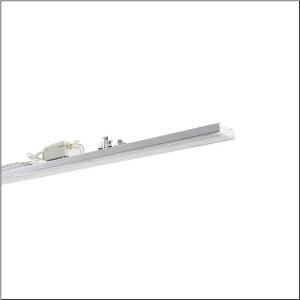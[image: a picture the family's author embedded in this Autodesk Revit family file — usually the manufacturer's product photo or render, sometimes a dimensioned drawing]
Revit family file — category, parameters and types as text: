
# Revit family: licross_r__21_recessed_ho_52tl18de47xm_4b87
name_source: partatom
category: Lighting Fixtures
units: mm (PartAtom-declared; Revit-internal decimal feet)

## family parameters
Cut with Voids When Loaded = No
Host = Face
Light Source = No
Part Type = Normal
Room Calculation Point = No
Round Connector Dimension = Use Diameter
Shared = No

## types (1)
- --- (1 x LED, 7420 lm, 44.1 W, 4000K)
    Apparent Load = 44 VA
    CIE Flux Codes = 75 94 99 100 100
    Color Rendering = 80
    Color Temperature = 4000K
    Default Elevation = 1800 mm
    Description = Licross® 21 Recessed HO, luminaire insert, of sheet steel, galvanised, coil coated, white, length: 750mm, width: 66mm, height: 67mm, LED rated luminous flux: 7.420lm, light colour: 840, control gear: DALI 2, with plug, 5-pole, with phase selection, mains connection: 220..240V, AC, 50/60Hz, rated input power: 44W, halogen-free wiring, primary light control with lens, of plastic, primary optical cover: cover, of PMMA, light emission: direct distribution, primary light characteristic: symmetric, protection rating (complete): IP40, insulation class (complete): insulation class I (protective earthing), certification: CE, ENEC, VDE, UKCA, protection symbol: D if used in an environment without relevant dust loads with corresponding accessories, impact resistance: IK06, permissible ambient temperature for indoor applications: -25..+30°C, corresponds to IFS (International Featured Standards) requirements for safety and quality in the food industry, reducing of maximum allowable ambient temperature of 5°C with ceiling mounting, LABS conformity tested according to VDMA 24364:2018-05, packaging unit: 1 piece
    Height = 58 mm
    Lamp = 1 x LED
    Lamp Light Flux = 7420 lm
    Lamp Power = 44.1 W
    Lamp count = 1
    Length = 750 mm
    Luminous efficacy = 168 lm/W
    Manufacturer = Siteco
    ModVariant = No
    Model = 52TL18DE47XM
    Mounting Place = Ceiling
    Mounting Type = Pendant
    Number of Poles = 1
    OnlyDefault = Yes
    Power Factor = 1
    Product Name = Licross® 21 Recessed HO
    Product group = luminaire insert
    ProductGroupID = 901
    Protection Class = Protection class I
    Protection Degree = IP 40
    RLX_Detail_Level = 1
    RLX_Emergency_Light_Flux = 0 lm
    RLX_Emergency_Type = 0
    RLX_Emergency_Type_DB = No
    RlxData = <blob elided: 29497 chars, md5=d3340f9e>
    Socket = socket
    Standby Power = 0 W
    System Light Flux = 7420 lm
    System Power = 44 W
    Type Comments = factory setting: luminous flux: 100 % | dim-lin: 254 | 484 mA
    Type Image = l_1296930.jpg
    URL = http://relux.com
    VarID = @adj_057413
    Voltage = 0 V
    Weight = 0.00 kg
    Width = 66 mm

## geometry (parser evidence)
native form markers: Blend x4, Sweep x11
no freeform markers — native parametric forms only
